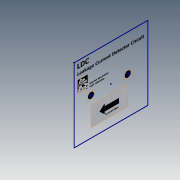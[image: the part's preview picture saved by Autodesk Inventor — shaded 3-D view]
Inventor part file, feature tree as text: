
AUTODESK INVENTOR PART (.ipt)
format: ipt  version: 2020.5 (Build 245400000, 400)  size: 169,472 bytes
history: native  units: mm
features: other x4, sketch x1
ambient origin geometry x8: Origin, YZ Plane, XZ Plane, XY Plane, X Axis, Y Axis, Z Axis, Center Point
feature tree (5):
  sketch  "Sketch30"  dims[d13=18.0mm d14=60.0mm d652=16.6mm d653=6.5mm d654=5.4mm d655=91.2mm d656=2.7mm d657=2.7mm d658=25.6mm d659=4.0mm d660=4.0mm d661=4.3mm d662=14.0mm d669=20.0mm d674=2.2mm d675=18.0mm d700=17.0mm d706=22.9mm d708=4.7mm d713=11.214mm d718=14.914mm d723=2.500231mm d724=2.500231mm d738=50.0mm d744=61.855mm d749=23.0mm d756=10.0mm d769=10.0mm d780=45.0mm d784=18.0mm d794=45.0mm d799=68.0mm]
  other  "Image7"
  other  "Image8"
  other  "Image9"
  other  "Image10"
